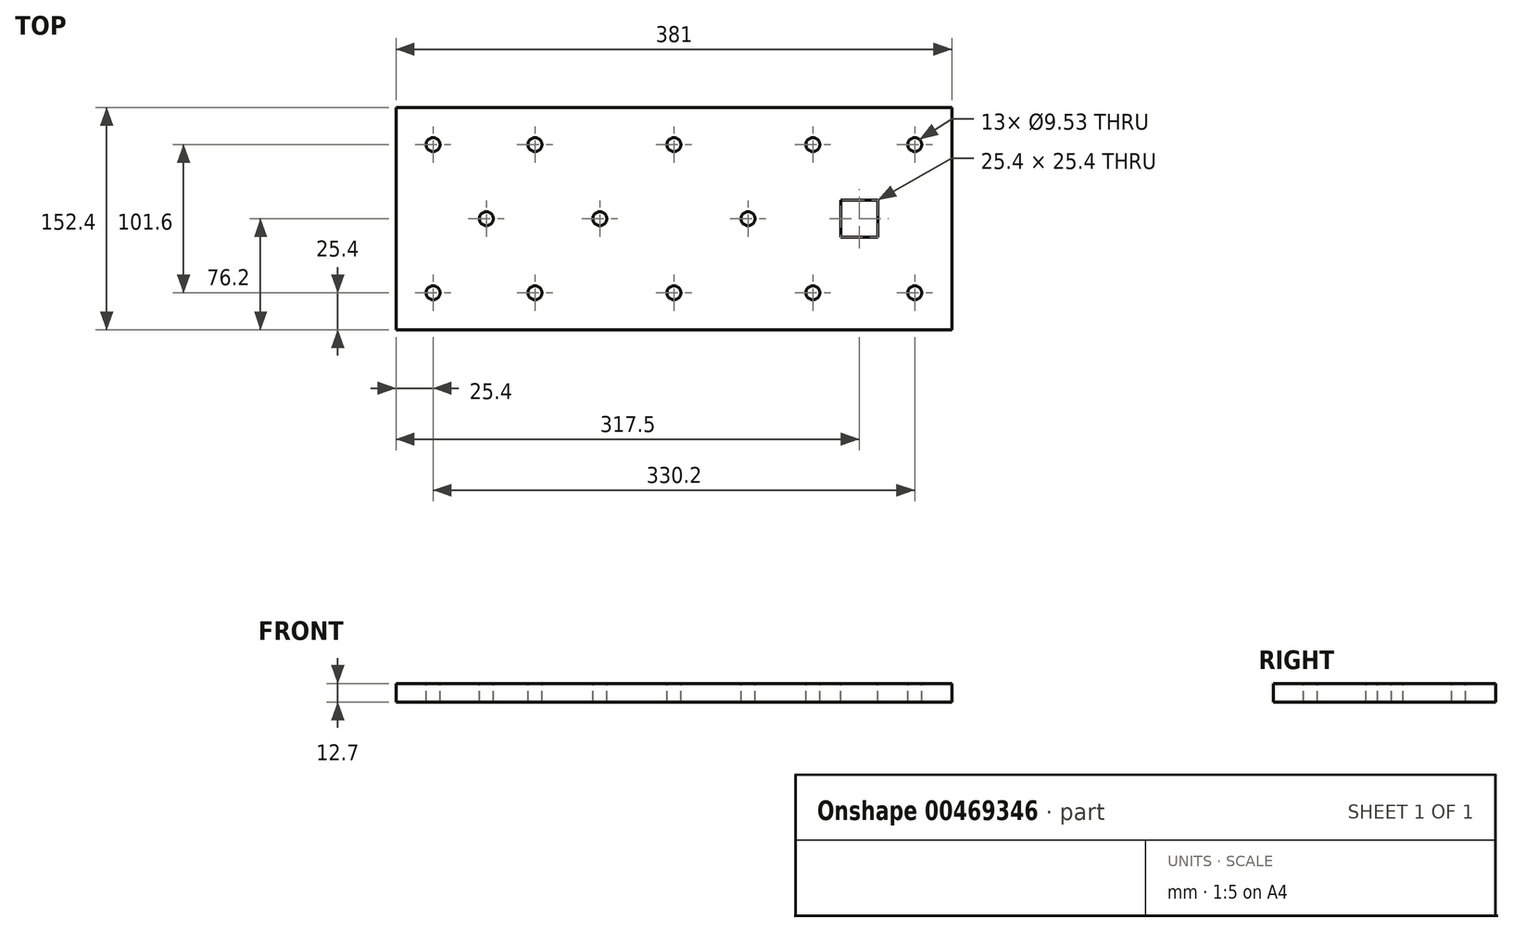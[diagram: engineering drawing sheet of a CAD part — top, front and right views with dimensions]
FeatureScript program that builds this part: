
annotation { "Feature Type Name" : "Feature", "Feature Type Description" : "" }
export const myFeature = defineFeature(function(context is Context, id is Id, definition is map)
    precondition{}
    {
        {
            var Q0;
            Q0=qCreatedBy(makeId("Top.planeOp"),FACE);
            var sketch = newSketch(context, id + "F0", { "sketchPlane" : qUnion([Q0])});
            skLineSegment(sketch, "E0.bottom", {"start": v(190.5, -76.2) * mm, "end": v(-190.5, -76.2) * mm});
            skLineSegment(sketch, "E0.top", {"start": v(190.5, 76.2) * mm, "end": v(-190.5, 76.2) * mm});
            skLineSegment(sketch, "E0.left", {"start": v(190.5, -76.2) * mm, "end": v(190.5, 76.2) * mm});
            skLineSegment(sketch, "E0.right", {"start": v(-190.5, -76.2) * mm, "end": v(-190.5, 76.2) * mm});
            skPoint(sketch, "E0.middle", {"position": v(0, 0) * mm});
            skSolve(sketch);
        }
        {
            var Q0;
            Q0 = qSketchRegion(id + "F0", true);
            extrude(context, id + "F1", {"entities" : qUnion([Q0]), "depth" : 12.7 * mm});
        }
        {
            var Q0;
            Q0=makeQuery(id+"F1.opExtrude","CAP_FACE",FACE,{"disambiguationData":[OSD([sQuery(id+"F0.wireOp",EDGE,"E0.bottom"),sQuery(id+"F0.wireOp",EDGE,"E0.top"),sQuery(id+"F0.wireOp",EDGE,"E0.left"),sQuery(id+"F0.wireOp",EDGE,"E0.right")])],"isStart":false});
            var sketch = newSketch(context, id + "F2", { "sketchPlane" : qUnion([Q0])});
            skPoint(sketch, "E1", {"position": v(-165.1, 50.8) * mm});
            skPoint(sketch, "E2.MirrorP", {"position": v(165.1, 50.8) * mm});
            skPoint(sketch, "E3.MirrorP", {"position": v(-165.1, -50.8) * mm});
            skPoint(sketch, "E4.MirrorP", {"position": v(165.1, -50.8) * mm});
            skPoint(sketch, "E5", {"position": v(-95.25, 50.8) * mm});
            skPoint(sketch, "E6.MirrorP", {"position": v(95.25, 50.8) * mm});
            skPoint(sketch, "E7.MirrorP", {"position": v(-95.25, -50.8) * mm});
            skPoint(sketch, "E8.MirrorP", {"position": v(95.25, -50.8) * mm});
            skPoint(sketch, "E9", {"position": v(0, 50.8) * mm});
            skPoint(sketch, "E10.MirrorP", {"position": v(0, -50.8) * mm});
            skPoint(sketch, "E11", {"position": v(-50.8, 0) * mm});
            skPoint(sketch, "E12.MirrorP", {"position": v(50.8, 0) * mm});
            skPoint(sketch, "E13", {"position": v(-128.59, 0) * mm});
            skPoint(sketch, "E14.MirrorP", {"position": v(128.59, 0) * mm});
            skSolve(sketch);
        }
        {
            var Q0;
            Q0=sQuery(id+"F2.wireOp",VERTEX,"E1");
            var Q1;
            Q1=makeQuery(id+"F1.opExtrude","SWEPT_BODY",BODY,{"disambiguationData":[OSD([sQuery(id+"F0.wireOp",EDGE,"E0.bottom"),sQuery(id+"F0.wireOp",EDGE,"E0.top"),sQuery(id+"F0.wireOp",EDGE,"E0.left"),sQuery(id+"F0.wireOp",EDGE,"E0.right")])]});
            hole(context, id + "F3", {"style" : HoleStyle.SIMPLE, "endStyle" : HoleEndStyle.THROUGH, "holeDiameter" : 9.52 * mm, "isTappedThrough" : true, "tappedDepth" : 12.7 * mm, "tapClearance" : 3, "locations" : qUnion([Q0]), "scope" : qUnion([Q1])});
        }
        {
            var Q0;
            Q0=sQuery(id+"F2.wireOp",VERTEX,"E5");
            var Q1;
            Q1=sQuery(id+"F2.wireOp",VERTEX,"E9");
            var Q2;
            Q2=sQuery(id+"F2.wireOp",VERTEX,"E6.MirrorP");
            var Q3;
            Q3=sQuery(id+"F2.wireOp",VERTEX,"E2.MirrorP");
            var Q4;
            Q4=sQuery(id+"F2.wireOp",VERTEX,"E14.MirrorP");
            var Q5;
            Q5=sQuery(id+"F2.wireOp",VERTEX,"E12.MirrorP");
            var Q6;
            Q6=sQuery(id+"F2.wireOp",VERTEX,"E11");
            var Q7;
            Q7=sQuery(id+"F2.wireOp",VERTEX,"E13");
            var Q8;
            Q8=sQuery(id+"F2.wireOp",VERTEX,"E3.MirrorP");
            var Q9;
            Q9=sQuery(id+"F2.wireOp",VERTEX,"E7.MirrorP");
            var Q10;
            Q10=sQuery(id+"F2.wireOp",VERTEX,"E10.MirrorP");
            var Q11;
            Q11=sQuery(id+"F2.wireOp",VERTEX,"E8.MirrorP");
            var Q12;
            Q12=sQuery(id+"F2.wireOp",VERTEX,"E4.MirrorP");
            var Q13;
            Q13=makeQuery(id+"F1.opExtrude","SWEPT_BODY",BODY,{"disambiguationData":[OSD([sQuery(id+"F0.wireOp",EDGE,"E0.bottom"),sQuery(id+"F0.wireOp",EDGE,"E0.top"),sQuery(id+"F0.wireOp",EDGE,"E0.left"),sQuery(id+"F0.wireOp",EDGE,"E0.right")])]});
            hole(context, id + "F4", {"style" : HoleStyle.SIMPLE, "endStyle" : HoleEndStyle.THROUGH, "holeDiameter" : 9.52 * mm, "isTappedThrough" : true, "tappedDepth" : 12.7 * mm, "tapClearance" : 3, "locations" : qUnion([Q0, Q1, Q2, Q3, Q4, Q5, Q6, Q7, Q8, Q9, Q10, Q11, Q12]), "scope" : qUnion([Q13])});
        }
        {
            var Q0;
            Q0=makeQuery(id+"F2.imprint","IMPRINT",FACE,{"disambiguationData":[TD([[makeQuery(id+"F2.imprint","IMPRINT",EDGE,{"derivedFrom":makeQuery(id+"F1.opExtrude","CAP_EDGE",EDGE,{"disambiguationData":[OSD([sQuery(id+"F0.wireOp",EDGE,"E0.bottom")])],"isStart":false})}),-1.0]])]});
            var sketch = newSketch(context, id + "F5", { "sketchPlane" : qUnion([Q0])});
            skLineSegment(sketch, "E15.bottom", {"start": v(114.3, 12.7) * mm, "end": v(139.7, 12.7) * mm});
            skLineSegment(sketch, "E15.top", {"start": v(114.3, -12.7) * mm, "end": v(139.7, -12.7) * mm});
            skLineSegment(sketch, "E15.left", {"start": v(114.3, 12.7) * mm, "end": v(114.3, -12.7) * mm});
            skLineSegment(sketch, "E15.right", {"start": v(139.7, 12.7) * mm, "end": v(139.7, -12.7) * mm});
            skPoint(sketch, "E15.middle", {"position": v(127, 0) * mm});
            skSolve(sketch);
        }
        {
            var Q0;
            Q0 = qSketchRegion(id + "F5", true);
            extrude(context, id + "F6", {"entities" : qUnion([Q0]), "operationType" : NewBodyOperationType.REMOVE, "oppositeDirection" : true, "depth" : 12.7 * mm});
        }
    });
